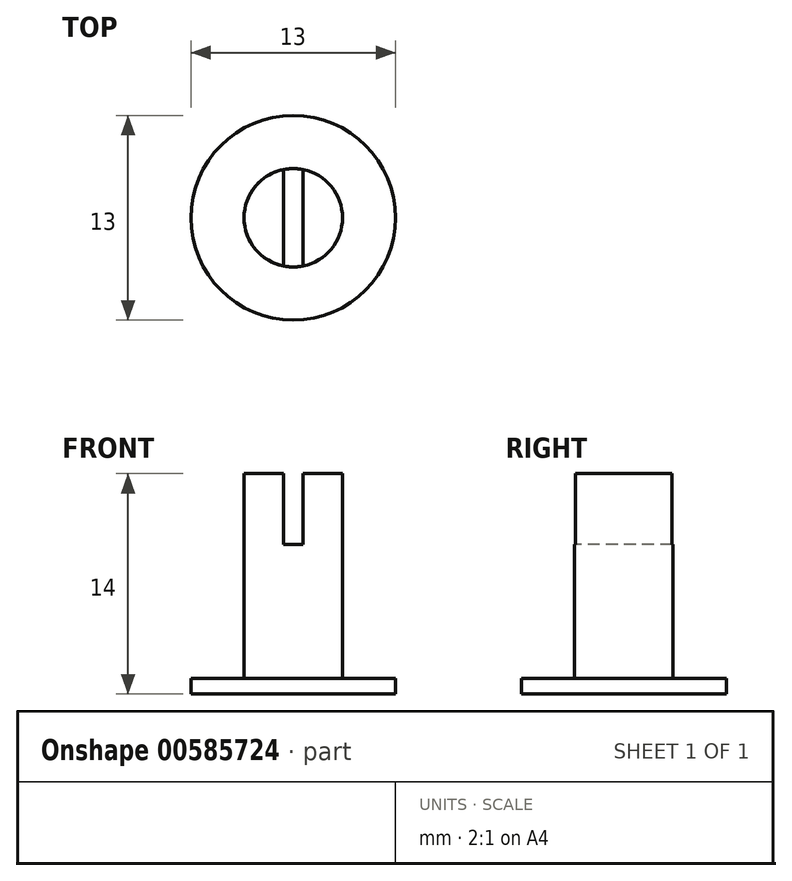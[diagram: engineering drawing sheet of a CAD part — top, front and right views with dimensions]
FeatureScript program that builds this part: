
annotation { "Feature Type Name" : "Feature", "Feature Type Description" : "" }
export const myFeature = defineFeature(function(context is Context, id is Id, definition is map)
    precondition{}
    {
        {
            var Q0;
            Q0=qCreatedBy(makeId("Top.planeOp"),FACE);
            var sketch = newSketch(context, id + "F0", { "sketchPlane" : qUnion([Q0])});
            skCircle(sketch, "E0", {"center": v(0, 0) * mm, "radius": 6.5 * mm});
            skCircle(sketch, "E1", {"center": v(0, 0) * mm, "radius": 3.12 * mm});
            skSolve(sketch);
        }
        {
            var Q0;
            Q0=makeQuery(id+"F0.imprint","IMPRINT",FACE,{"disambiguationData":[TD([[makeQuery(id+"F0.imprint","IMPRINT",EDGE,{"derivedFrom":sQuery(id+"F0.wireOp",EDGE,"E1")}),1.0]])]});
            extrude(context, id + "F1", {"entities" : qUnion([Q0]), "depth" : 14 * mm, "offsetDistance" : 25 * mm});
        }
        {
            var Q0;
            Q0 = qSketchRegion(id + "F0", true);
            extrude(context, id + "F2", {"entities" : qUnion([Q0]), "operationType" : NewBodyOperationType.ADD, "depth" : 1 * mm, "offsetDistance" : 25 * mm});
        }
        {
            var Q0;
            Q0=makeQuery(id+"F1.opExtrude","CAP_FACE",FACE,{"disambiguationData":[OSD([sQuery(id+"F0.wireOp",EDGE,"E1")])],"isStart":false});
            var sketch = newSketch(context, id + "F3", { "sketchPlane" : qUnion([Q0])});
            skLineSegment(sketch, "E2.bottom", {"start": v(0.63, 3.54) * mm, "end": v(-0.62, 3.54) * mm});
            skLineSegment(sketch, "E2.top", {"start": v(0.62, -3.54) * mm, "end": v(-0.63, -3.54) * mm});
            skLineSegment(sketch, "E2.left", {"start": v(0.63, 3.54) * mm, "end": v(0.62, -3.54) * mm});
            skLineSegment(sketch, "E2.right", {"start": v(-0.62, 3.54) * mm, "end": v(-0.63, -3.54) * mm});
            skPoint(sketch, "E2.middle", {"position": v(0, 0) * mm});
            skSolve(sketch);
        }
        {
            var Q0;
            {var subQ0=sQuery(id+"F3.wireOp",EDGE,"E2.left");var subQ1=makeQuery(id+"F1.opExtrude","CAP_EDGE",EDGE,{"disambiguationData":[OSD([sQuery(id+"F0.wireOp",EDGE,"E1")])],"isStart":false});var subQ2=makeQuery(id+"F3.imprint","INTERSECT",VERTEX,{"disambiguationData":[OD(0.0)],"derivedFrom":[subQ1,subQ0]});Q0=makeQuery(id+"F3.imprint","IMPRINT",FACE,{"disambiguationData":[TD([[makeQuery(id+"F3.imprint","IMPRINT",EDGE,{"disambiguationData":[TD([[subQ2,-1.0]])],"derivedFrom":subQ0}),-1.0]])]});}
            extrude(context, id + "F4", {"entities" : qUnion([Q0]), "operationType" : NewBodyOperationType.REMOVE, "oppositeDirection" : true, "depth" : 4.5 * mm, "offsetDistance" : 25 * mm});
        }
    });
